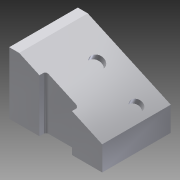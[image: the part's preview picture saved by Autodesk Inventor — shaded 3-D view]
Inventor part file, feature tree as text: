
AUTODESK INVENTOR PART (.ipt)
format: ipt  version: 2015 (Build 190159000, 159)  size: 152,064 bytes
history: native  units: in
note: dims shown in document units (in); Inventor stores cm internally (conversion verified against a paired STEP export)
features: sketch x4, extrude x3, shell x1
ambient origin geometry x8: Origin, YZ Plane, XZ Plane, XY Plane, X Axis, Y Axis, Z Axis, Center Point
bodies: Solid1 (feature_tree)
feature tree (8):
  extrude  "Extrusion1"  TaperAngle=0.0deg  [1 undecoded]
  extrude  "Extrusion2"  TaperAngle=0.0deg  [1 undecoded]
  sketch  "Sketch3"  dims[d19=1.225in d20=0.25in d21=1.1375in d22=0.0938in d23=3.5in d24=0.375in d25=2.3333in d26=0.0in]
  extrude  "Extrusion3"  Depth=0.2188in
  shell  "Shell1"  Thickness=0.0in
  sketch  "Sketch1"  dims[d5=0.0in d14=0.0in]
  sketch  "Sketch2"  dims[d18=0.0938in]
  sketch  "Sketch4"  dims[d27=0.0in d28=0.2188in d29=0.0in]
note: 2 required parameter values undecoded (feature->parameter linkage not recoverable at this tier; creation-order binding heuristic only, values carry confidence <= 0.55)
